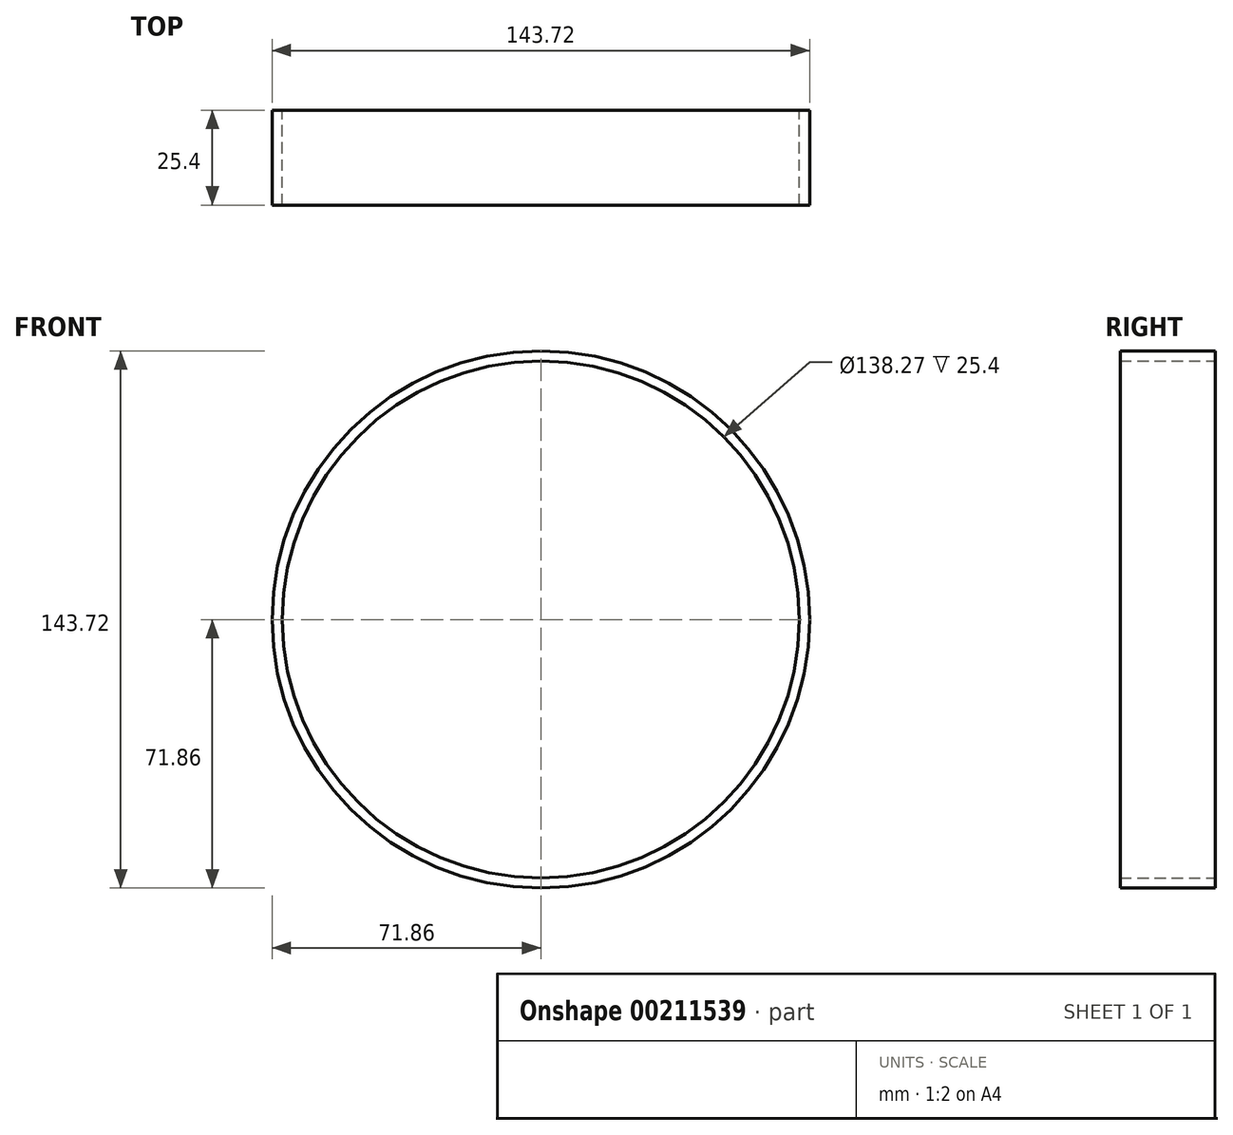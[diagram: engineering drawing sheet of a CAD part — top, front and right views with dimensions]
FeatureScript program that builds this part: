
annotation { "Feature Type Name" : "Feature", "Feature Type Description" : "" }
export const myFeature = defineFeature(function(context is Context, id is Id, definition is map)
    precondition{}
    {
        {
            var Q0;
            Q0=qCreatedBy(makeId("Front.planeOp"),FACE);
            var sketch = newSketch(context, id + "F0", { "sketchPlane" : qUnion([Q0])});
            skCircle(sketch, "E0", {"center": v(0, 0) * mm, "radius": 71.86 * mm});
            skSolve(sketch);
        }
        {
            var Q0;
            Q0=qCreatedBy(makeId("Front.planeOp"),FACE);
            var sketch = newSketch(context, id + "F1", { "sketchPlane" : qUnion([Q0])});
            skCircle(sketch, "E1", {"center": v(0, 0) * mm, "radius": 69.14 * mm});
            skSolve(sketch);
        }
        {
            var Q0;
            Q0=makeQuery(id+"F0.imprint","IMPRINT",FACE,{"disambiguationData":[TD([[makeQuery(id+"F0.imprint","IMPRINT",EDGE,{"derivedFrom":sQuery(id+"F0.wireOp",EDGE,"E0")}),1.0]])]});
            extrude(context, id + "F2", {"entities" : qUnion([Q0]), "depth" : 25.4 * mm});
        }
        {
            var Q0;
            Q0=makeQuery(id+"F1.imprint","IMPRINT",FACE,{"disambiguationData":[TD([[makeQuery(id+"F1.imprint","IMPRINT",EDGE,{"derivedFrom":sQuery(id+"F1.wireOp",EDGE,"E1")}),1.0]])]});
            extrude(context, id + "F3", {"entities" : qUnion([Q0]), "operationType" : NewBodyOperationType.REMOVE, "depth" : 38.35 * mm});
        }
    });
